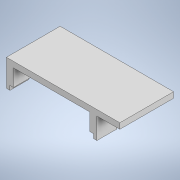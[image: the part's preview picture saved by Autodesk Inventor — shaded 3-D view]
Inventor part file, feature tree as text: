
AUTODESK INVENTOR PART (.ipt)
format: ipt  version: 2020.1 (Build 241239000, 239)  size: 142,848 bytes
history: native  units: mm
features: extrude x3, sketch x3, other x1
ambient origin geometry x8: Origin, YZ Plane, XZ Plane, XY Plane, X Axis, Y Axis, Z Axis, Center Point
bodies: Body1 (feature_tree)
feature tree (7):
  other  "Твердое тело1"
  extrude  "Выдавливание1"  Depth=15.0mm TaperAngle=0.0deg
  extrude  "Выдавливание2"  Depth=25.0mm
  extrude  "Выдавливание3"  Depth=25.0mm
  sketch  "Эскиз1"
  sketch  "Эскиз2"
  sketch  "Эскиз3"
